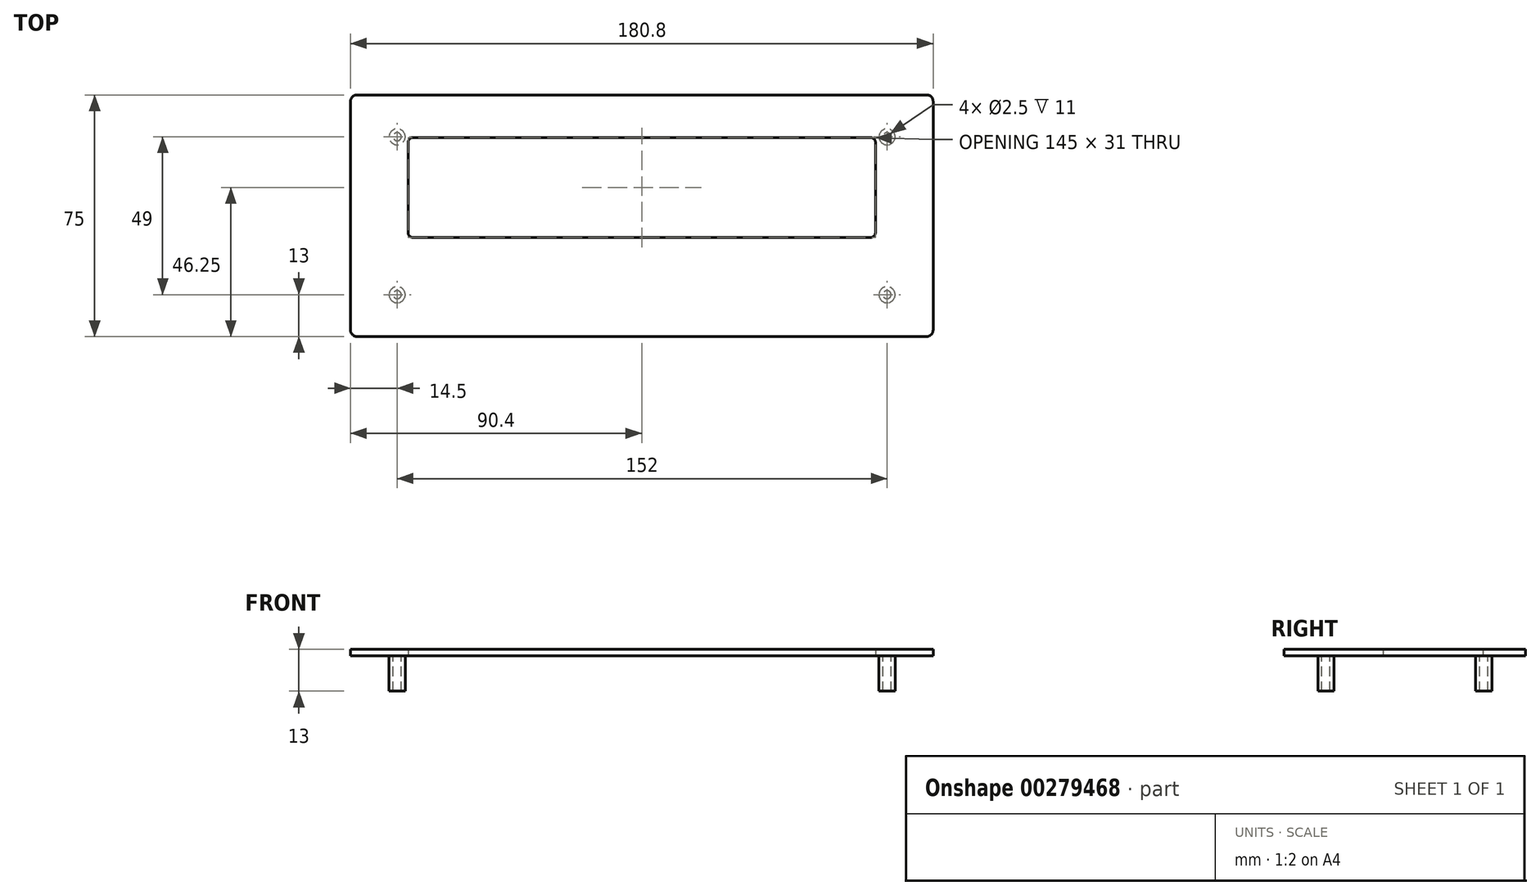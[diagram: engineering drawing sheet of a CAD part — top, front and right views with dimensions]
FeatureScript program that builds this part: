
annotation { "Feature Type Name" : "Feature", "Feature Type Description" : "" }
export const myFeature = defineFeature(function(context is Context, id is Id, definition is map)
    precondition{}
    {
        {
            var Q0;
            Q0=qCreatedBy(makeId("Top.planeOp"),FACE);
            var sketch = newSketch(context, id + "F0", { "sketchPlane" : qUnion([Q0])});
            skLineSegment(sketch, "E0.bottom", {"start": v(2, 0) * mm, "end": v(178.8, 0) * mm});
            skLineSegment(sketch, "E0.top", {"start": v(2, 75) * mm, "end": v(178.8, 75) * mm});
            skLineSegment(sketch, "E0.left", {"start": v(0, 2) * mm, "end": v(0, 73) * mm});
            skLineSegment(sketch, "E0.right", {"start": v(180.8, 2) * mm, "end": v(180.8, 73) * mm});
            skPoint(sketch, "E1.visualSharp", {"position": v(0, 75) * mm});
            skArc(sketch, "E1.filletArc", {"start": v(2, 75) * mm, "mid": v(0.59, 74.41) * mm, "end": v(0, 73) * mm});
            skPoint(sketch, "E2.visualSharp", {"position": v(180.8, 75) * mm});
            skArc(sketch, "E2.filletArc", {"start": v(180.8, 73) * mm, "mid": v(180.21, 74.41) * mm, "end": v(178.8, 75) * mm});
            skPoint(sketch, "E3.visualSharp", {"position": v(180.8, 0) * mm});
            skArc(sketch, "E3.filletArc", {"start": v(178.8, 0) * mm, "mid": v(180.21, 0.59) * mm, "end": v(180.8, 2) * mm});
            skPoint(sketch, "E4.visualSharp", {"position": v(0, 0) * mm});
            skArc(sketch, "E4.filletArc", {"start": v(0, 2) * mm, "mid": v(0.59, 0.59) * mm, "end": v(2, 0) * mm});
            skLineSegment(sketch, "E5.bottom", {"start": v(19.4, 61.75) * mm, "end": v(161.4, 61.75) * mm});
            skLineSegment(sketch, "E5.top", {"start": v(19.4, 30.75) * mm, "end": v(161.4, 30.75) * mm});
            skLineSegment(sketch, "E5.left", {"start": v(17.9, 60.25) * mm, "end": v(17.9, 32.25) * mm});
            skLineSegment(sketch, "E5.right", {"start": v(162.9, 60.25) * mm, "end": v(162.9, 32.25) * mm});
            skLineSegment(sketch, "E6", {"start": v(90.4, 75) * mm, "end": v(90.4, 61.75) * mm, "construction": true});
            skPoint(sketch, "E6.endSnap0", {"position": v(90.4, 61.75) * mm});
            skPoint(sketch, "E7.visualSharp", {"position": v(17.9, 61.75) * mm});
            skArc(sketch, "E7.filletArc", {"start": v(19.4, 61.75) * mm, "mid": v(18.34, 61.31) * mm, "end": v(17.9, 60.25) * mm});
            skPoint(sketch, "E8.visualSharp", {"position": v(162.9, 61.75) * mm});
            skArc(sketch, "E8.filletArc", {"start": v(162.9, 60.25) * mm, "mid": v(162.46, 61.31) * mm, "end": v(161.4, 61.75) * mm});
            skPoint(sketch, "E9.visualSharp", {"position": v(162.9, 30.75) * mm});
            skArc(sketch, "E9.filletArc", {"start": v(161.4, 30.75) * mm, "mid": v(162.46, 31.19) * mm, "end": v(162.9, 32.25) * mm});
            skPoint(sketch, "E10.visualSharp", {"position": v(17.9, 30.75) * mm});
            skArc(sketch, "E10.filletArc", {"start": v(17.9, 32.25) * mm, "mid": v(18.34, 31.19) * mm, "end": v(19.4, 30.75) * mm});
            skSolve(sketch);
        }
        {
            var Q0;
            Q0=makeQuery(id+"F0.imprint","IMPRINT",FACE,{"disambiguationData":[TD([[makeQuery(id+"F0.imprint","IMPRINT",EDGE,{"derivedFrom":sQuery(id+"F0.wireOp",EDGE,"E0.bottom")}),1.0]])]});
            extrude(context, id + "F1", {"entities" : qUnion([Q0]), "depth" : 2 * mm});
        }
        {
            var Q0;
            Q0=makeQuery(id+"F1.opExtrude","CAP_FACE",FACE,{"disambiguationData":[OSD([sQuery(id+"F0.wireOp",EDGE,"E0.bottom"),sQuery(id+"F0.wireOp",EDGE,"E0.top"),sQuery(id+"F0.wireOp",EDGE,"E0.left"),sQuery(id+"F0.wireOp",EDGE,"E0.right"),sQuery(id+"F0.wireOp",EDGE,"E1.filletArc"),sQuery(id+"F0.wireOp",EDGE,"E2.filletArc"),sQuery(id+"F0.wireOp",EDGE,"E3.filletArc"),sQuery(id+"F0.wireOp",EDGE,"E4.filletArc"),sQuery(id+"F0.wireOp",EDGE,"E5.bottom"),sQuery(id+"F0.wireOp",EDGE,"E5.top"),sQuery(id+"F0.wireOp",EDGE,"E5.left"),sQuery(id+"F0.wireOp",EDGE,"E5.right"),sQuery(id+"F0.wireOp",EDGE,"E7.filletArc"),sQuery(id+"F0.wireOp",EDGE,"E8.filletArc"),sQuery(id+"F0.wireOp",EDGE,"E9.filletArc"),sQuery(id+"F0.wireOp",EDGE,"E10.filletArc")])],"isStart":true});
            var sketch = newSketch(context, id + "F2", { "sketchPlane" : qUnion([Q0])});
            skCircle(sketch, "E11", {"center": v(14.5, -62) * mm, "radius": 1.25 * mm});
            skCircle(sketch, "E12", {"center": v(14.5, -62) * mm, "radius": 2.5 * mm});
            skCircle(sketch, "E13.0.1.0", {"center": v(14.5, -13) * mm, "radius": 2.5 * mm});
            skCircle(sketch, "E13.0.1.1", {"center": v(14.5, -13) * mm, "radius": 1.25 * mm});
            skCircle(sketch, "E13.1.0.0", {"center": v(166.5, -62) * mm, "radius": 2.5 * mm});
            skCircle(sketch, "E13.1.0.1", {"center": v(166.5, -62) * mm, "radius": 1.25 * mm});
            skCircle(sketch, "E13.1.1.0", {"center": v(166.5, -13) * mm, "radius": 2.5 * mm});
            skCircle(sketch, "E13.1.1.1", {"center": v(166.5, -13) * mm, "radius": 1.25 * mm});
            skLineSegment(sketch, "E13.direction1", {"start": v(14.5, -62) * mm, "end": v(166.5, -62) * mm, "construction": true});
            skLineSegment(sketch, "E13.direction2", {"start": v(14.5, -62) * mm, "end": v(14.5, -13) * mm, "construction": true});
            skSolve(sketch);
        }
        {
            var Q0;
            Q0=makeQuery(id+"F2.imprint","IMPRINT",FACE,{"disambiguationData":[TD([[makeQuery(id+"F2.imprint","IMPRINT",EDGE,{"derivedFrom":sQuery(id+"F2.wireOp",EDGE,"E13.0.1.0")}),1.0]])]});
            var Q1;
            Q1=makeQuery(id+"F2.imprint","IMPRINT",FACE,{"disambiguationData":[TD([[makeQuery(id+"F2.imprint","IMPRINT",EDGE,{"derivedFrom":sQuery(id+"F2.wireOp",EDGE,"E11")}),-1.0]])]});
            var Q2;
            Q2=makeQuery(id+"F2.imprint","IMPRINT",FACE,{"disambiguationData":[TD([[makeQuery(id+"F2.imprint","IMPRINT",EDGE,{"derivedFrom":sQuery(id+"F2.wireOp",EDGE,"E13.1.0.0")}),1.0]])]});
            var Q3;
            Q3=makeQuery(id+"F2.imprint","IMPRINT",FACE,{"disambiguationData":[TD([[makeQuery(id+"F2.imprint","IMPRINT",EDGE,{"derivedFrom":sQuery(id+"F2.wireOp",EDGE,"E13.1.1.0")}),1.0]])]});
            extrude(context, id + "F3", {"entities" : qUnion([Q0, Q1, Q2, Q3]), "operationType" : NewBodyOperationType.ADD, "depth" : 11 * mm});
        }
    });
